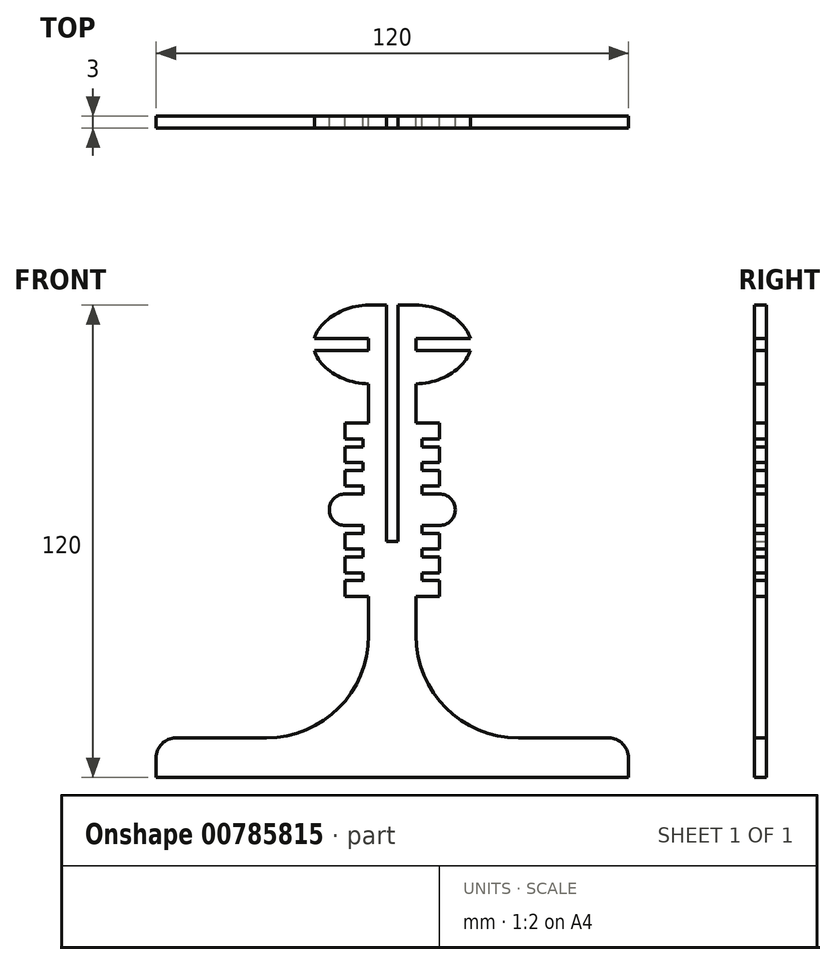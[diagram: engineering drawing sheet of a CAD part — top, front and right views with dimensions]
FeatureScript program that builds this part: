
annotation { "Feature Type Name" : "Feature", "Feature Type Description" : "" }
export const myFeature = defineFeature(function(context is Context, id is Id, definition is map)
    precondition{}
    {
        {
            var Q0;
            Q0=qCreatedBy(makeId("Front.planeOp"),FACE);
            var sketch = newSketch(context, id + "F0", { "sketchPlane" : qUnion([Q0])});
            skLineSegment(sketch, "E0", {"start": v(-60, 0) * mm, "end": v(60, 0) * mm});
            skLineSegment(sketch, "E1", {"start": v(60, 0) * mm, "end": v(60, 5) * mm});
            skLineSegment(sketch, "E2", {"start": v(55, 10) * mm, "end": v(32, 10) * mm});
            skLineSegment(sketch, "E3", {"start": v(6, 36) * mm, "end": v(6, 100) * mm});
            skLineSegment(sketch, "E4", {"start": v(1.5, 120) * mm, "end": v(1.5, 60) * mm});
            skLineSegment(sketch, "E5", {"start": v(1.5, 60) * mm, "end": v(-1.5, 60) * mm});
            skLineSegment(sketch, "E6", {"start": v(-1.5, 60) * mm, "end": v(-1.5, 120) * mm});
            skLineSegment(sketch, "E7", {"start": v(-6, 100) * mm, "end": v(-6, 36) * mm});
            skLineSegment(sketch, "E8", {"start": v(-32, 10) * mm, "end": v(-55, 10) * mm});
            skLineSegment(sketch, "E9", {"start": v(-60, 5) * mm, "end": v(-60, 0) * mm});
            skLineSegment(sketch, "E10", {"start": v(-1.5, 120) * mm, "end": v(-6, 120) * mm});
            skLineSegment(sketch, "E11", {"start": v(1.5, 120) * mm, "end": v(6, 120) * mm});
            skFitSpline(sketch, "E12", {"points": [v(-6, 120) * mm, v(-20, 110) * mm, v(-6, 100) * mm], "startDerivative": vector(-42.6, 0) * mm, "endDerivative": vector(42.6, 0.15) * mm});
            skLineSegment(sketch, "E13", {"start": v(-20, 110) * mm, "end": v(-6, 110) * mm});
            skLineSegment(sketch, "E14", {"start": v(-6, 100) * mm, "end": v(-1.5, 100) * mm});
            skLineSegment(sketch, "E15", {"start": v(-6, 90) * mm, "end": v(-12, 90) * mm});
            skLineSegment(sketch, "E16", {"start": v(-12, 90) * mm, "end": v(-12, 86) * mm});
            skLineSegment(sketch, "E17", {"start": v(-12, 86) * mm, "end": v(-7.5, 86) * mm});
            skLineSegment(sketch, "E18", {"start": v(-7.5, 86) * mm, "end": v(-7.5, 84) * mm});
            skLineSegment(sketch, "E19", {"start": v(-7.5, 84) * mm, "end": v(-12, 84) * mm});
            skLineSegment(sketch, "E20", {"start": v(-12, 84) * mm, "end": v(-12, 80) * mm});
            skLineSegment(sketch, "E21", {"start": v(-12, 80) * mm, "end": v(-7.5, 80) * mm});
            skLineSegment(sketch, "E22", {"start": v(-7.5, 80) * mm, "end": v(-7.5, 78) * mm});
            skLineSegment(sketch, "E23", {"start": v(-7.5, 78) * mm, "end": v(-12, 78) * mm});
            skLineSegment(sketch, "E24", {"start": v(-12, 78) * mm, "end": v(-12, 74) * mm});
            skLineSegment(sketch, "E25", {"start": v(-12, 74) * mm, "end": v(-7.5, 74) * mm});
            skLineSegment(sketch, "E26", {"start": v(-7.5, 74) * mm, "end": v(-7.5, 72) * mm});
            skLineSegment(sketch, "E27", {"start": v(-7.5, 72) * mm, "end": v(-12, 72) * mm});
            skLineSegment(sketch, "E28", {"start": v(-12, 72) * mm, "end": v(-12, 68) * mm});
            skLineSegment(sketch, "E29", {"start": v(-12, 68) * mm, "end": v(-6, 68) * mm});
            skArc(sketch, "E30", {"start": v(-32, 10) * mm, "mid": v(-13.62, 17.62) * mm, "end": v(-6, 36) * mm});
            skLineSegment(sketch, "E31.MirrorCS", {"start": v(-12, 64) * mm, "end": v(-12, 68) * mm});
            skLineSegment(sketch, "E32.MirrorCS", {"start": v(-7.5, 64) * mm, "end": v(-12, 64) * mm});
            skLineSegment(sketch, "E33.MirrorCS", {"start": v(-7.5, 62) * mm, "end": v(-7.5, 64) * mm});
            skLineSegment(sketch, "E34.MirrorCS", {"start": v(-12, 62) * mm, "end": v(-7.5, 62) * mm});
            skLineSegment(sketch, "E35.MirrorCS", {"start": v(-12, 58) * mm, "end": v(-12, 62) * mm});
            skLineSegment(sketch, "E36.MirrorCS", {"start": v(-7.5, 58) * mm, "end": v(-12, 58) * mm});
            skLineSegment(sketch, "E37.MirrorCS", {"start": v(-7.5, 56) * mm, "end": v(-7.5, 58) * mm});
            skLineSegment(sketch, "E38.MirrorCS", {"start": v(-12, 56) * mm, "end": v(-7.5, 56) * mm});
            skLineSegment(sketch, "E39.MirrorCS", {"start": v(-12, 52) * mm, "end": v(-12, 56) * mm});
            skLineSegment(sketch, "E40.MirrorCS", {"start": v(-7.5, 52) * mm, "end": v(-12, 52) * mm});
            skLineSegment(sketch, "E41.MirrorCS", {"start": v(-7.5, 50) * mm, "end": v(-7.5, 52) * mm});
            skLineSegment(sketch, "E42.MirrorCS", {"start": v(-12, 50) * mm, "end": v(-7.5, 50) * mm});
            skLineSegment(sketch, "E43.MirrorCS", {"start": v(-12, 46) * mm, "end": v(-12, 50) * mm});
            skLineSegment(sketch, "E44.MirrorCS", {"start": v(-6, 46) * mm, "end": v(-12, 46) * mm});
            skPoint(sketch, "E45.visualSharp", {"position": v(-60, 10) * mm});
            skArc(sketch, "E45.filletArc", {"start": v(-55, 10) * mm, "mid": v(-58.54, 8.54) * mm, "end": v(-60, 5) * mm});
            skArc(sketch, "E46.MirrorCS", {"start": v(32, 10) * mm, "mid": v(13.62, 17.62) * mm, "end": v(6, 36) * mm});
            skFitSpline(sketch, "E47.MirrorCS", {"points": [v(6, 120) * mm, v(20, 110) * mm, v(6, 100) * mm], "startDerivative": vector(42.6, 0) * mm, "endDerivative": vector(-42.6, 0.15) * mm});
            skLineSegment(sketch, "E48.MirrorCS", {"start": v(6, 46) * mm, "end": v(12, 46) * mm});
            skLineSegment(sketch, "E49.MirrorCS", {"start": v(12, 46) * mm, "end": v(12, 50) * mm});
            skLineSegment(sketch, "E50.MirrorCS", {"start": v(12, 50) * mm, "end": v(7.5, 50) * mm});
            skLineSegment(sketch, "E51.MirrorCS", {"start": v(7.5, 50) * mm, "end": v(7.5, 52) * mm});
            skLineSegment(sketch, "E52.MirrorCS", {"start": v(7.5, 52) * mm, "end": v(12, 52) * mm});
            skLineSegment(sketch, "E53.MirrorCS", {"start": v(12, 52) * mm, "end": v(12, 56) * mm});
            skLineSegment(sketch, "E54.MirrorCS", {"start": v(12, 56) * mm, "end": v(7.5, 56) * mm});
            skLineSegment(sketch, "E55.MirrorCS", {"start": v(7.5, 56) * mm, "end": v(7.5, 58) * mm});
            skLineSegment(sketch, "E56.MirrorCS", {"start": v(7.5, 58) * mm, "end": v(12, 58) * mm});
            skLineSegment(sketch, "E57.MirrorCS", {"start": v(12, 58) * mm, "end": v(12, 62) * mm});
            skLineSegment(sketch, "E58.MirrorCS", {"start": v(12, 62) * mm, "end": v(7.5, 62) * mm});
            skLineSegment(sketch, "E59.MirrorCS", {"start": v(7.5, 62) * mm, "end": v(7.5, 64) * mm});
            skLineSegment(sketch, "E60.MirrorCS", {"start": v(7.5, 64) * mm, "end": v(12, 64) * mm});
            skLineSegment(sketch, "E61.MirrorCS", {"start": v(12, 64) * mm, "end": v(12, 68) * mm});
            skLineSegment(sketch, "E62.MirrorCS", {"start": v(12, 72) * mm, "end": v(12, 68) * mm});
            skLineSegment(sketch, "E63.MirrorCS", {"start": v(7.5, 72) * mm, "end": v(12, 72) * mm});
            skLineSegment(sketch, "E64.MirrorCS", {"start": v(7.5, 74) * mm, "end": v(7.5, 72) * mm});
            skLineSegment(sketch, "E65.MirrorCS", {"start": v(12, 74) * mm, "end": v(7.5, 74) * mm});
            skLineSegment(sketch, "E66.MirrorCS", {"start": v(12, 78) * mm, "end": v(12, 74) * mm});
            skLineSegment(sketch, "E67.MirrorCS", {"start": v(7.5, 78) * mm, "end": v(12, 78) * mm});
            skLineSegment(sketch, "E68.MirrorCS", {"start": v(7.5, 80) * mm, "end": v(7.5, 78) * mm});
            skLineSegment(sketch, "E69.MirrorCS", {"start": v(12, 80) * mm, "end": v(7.5, 80) * mm});
            skLineSegment(sketch, "E70.MirrorCS", {"start": v(12, 84) * mm, "end": v(12, 80) * mm});
            skLineSegment(sketch, "E71.MirrorCS", {"start": v(7.5, 84) * mm, "end": v(12, 84) * mm});
            skLineSegment(sketch, "E72.MirrorCS", {"start": v(7.5, 86) * mm, "end": v(7.5, 84) * mm});
            skLineSegment(sketch, "E73.MirrorCS", {"start": v(12, 86) * mm, "end": v(7.5, 86) * mm});
            skLineSegment(sketch, "E74.MirrorCS", {"start": v(12, 90) * mm, "end": v(12, 86) * mm});
            skLineSegment(sketch, "E75.MirrorCS", {"start": v(6, 90) * mm, "end": v(12, 90) * mm});
            skPoint(sketch, "E76.visualSharp", {"position": v(60, 0) * mm});
            skPoint(sketch, "E77.visualSharp", {"position": v(60, 10) * mm});
            skArc(sketch, "E77.filletArc", {"start": v(60, 5) * mm, "mid": v(58.54, 8.54) * mm, "end": v(55, 10) * mm});
            skArc(sketch, "E78", {"start": v(-12, 72) * mm, "mid": v(-16, 68) * mm, "end": v(-12, 64) * mm});
            skArc(sketch, "E79.MirrorCS", {"start": v(12, 72) * mm, "mid": v(16, 68) * mm, "end": v(12, 64) * mm});
            skLineSegment(sketch, "E80", {"start": v(-6, 111.5) * mm, "end": v(-6, 108.5) * mm});
            skLineSegment(sketch, "E81", {"start": v(-6, 108.5) * mm, "end": v(-19.8, 108.5) * mm});
            skLineSegment(sketch, "E82", {"start": v(-6, 111.5) * mm, "end": v(-19.8, 111.5) * mm});
            skLineSegment(sketch, "E83.MirrorCS", {"start": v(6, 108.5) * mm, "end": v(19.8, 108.5) * mm});
            skLineSegment(sketch, "E84.MirrorCS", {"start": v(6, 111.5) * mm, "end": v(6, 108.5) * mm});
            skLineSegment(sketch, "E85.MirrorCS", {"start": v(6, 111.5) * mm, "end": v(19.8, 111.5) * mm});
            skSolve(sketch);
        }
        {
            var Q0;
            Q0=makeQuery(id+"F0.imprint","IMPRINT",FACE,{"disambiguationData":[TD([[makeQuery(id+"F0.imprint","IMPRINT",EDGE,{"derivedFrom":sQuery(id+"F0.wireOp",EDGE,"E0")}),1.0]])]});
            var Q1;
            {var subQ1=sQuery(id+"F0.wireOp",EDGE,"E10");Q1=makeQuery(id+"F0.imprint","IMPRINT",FACE,{"disambiguationData":[TD([[makeQuery(id+"F0.imprint","IMPRINT",EDGE,{"derivedFrom":subQ1}),1.0]])]});}
            var Q2;
            {var subQ0=sQuery(id+"F0.wireOp",EDGE,"E15");Q2=makeQuery(id+"F0.imprint","IMPRINT",FACE,{"disambiguationData":[TD([[makeQuery(id+"F0.imprint","IMPRINT",EDGE,{"derivedFrom":subQ0}),1.0]])]});}
            var Q3;
            {var subQ0=sQuery(id+"F0.wireOp",EDGE,"E29");Q3=makeQuery(id+"F0.imprint","IMPRINT",FACE,{"disambiguationData":[TD([[makeQuery(id+"F0.imprint","IMPRINT",EDGE,{"derivedFrom":subQ0}),-1.0]])]});}
            var Q4;
            Q4=makeQuery(id+"F0.imprint","IMPRINT",FACE,{"disambiguationData":[TD([[makeQuery(id+"F0.imprint","IMPRINT",EDGE,{"derivedFrom":sQuery(id+"F0.wireOp",EDGE,"E28")}),-1.0]])]});
            var Q5;
            Q5=makeQuery(id+"F0.imprint","IMPRINT",FACE,{"disambiguationData":[TD([[makeQuery(id+"F0.imprint","IMPRINT",EDGE,{"derivedFrom":sQuery(id+"F0.wireOp",EDGE,"E61.MirrorCS")}),-1.0]])]});
            var Q6;
            {var subQ0=sQuery(id+"F0.wireOp",EDGE,"E48.MirrorCS");Q6=makeQuery(id+"F0.imprint","IMPRINT",FACE,{"disambiguationData":[TD([[makeQuery(id+"F0.imprint","IMPRINT",EDGE,{"derivedFrom":subQ0}),1.0]])]});}
            extrude(context, id + "F1", {"entities" : qUnion([Q0, Q1, Q2, Q3, Q4, Q5, Q6]), "depth" : 3 * mm, "offsetDistance" : 25 * mm});
        }
    });
